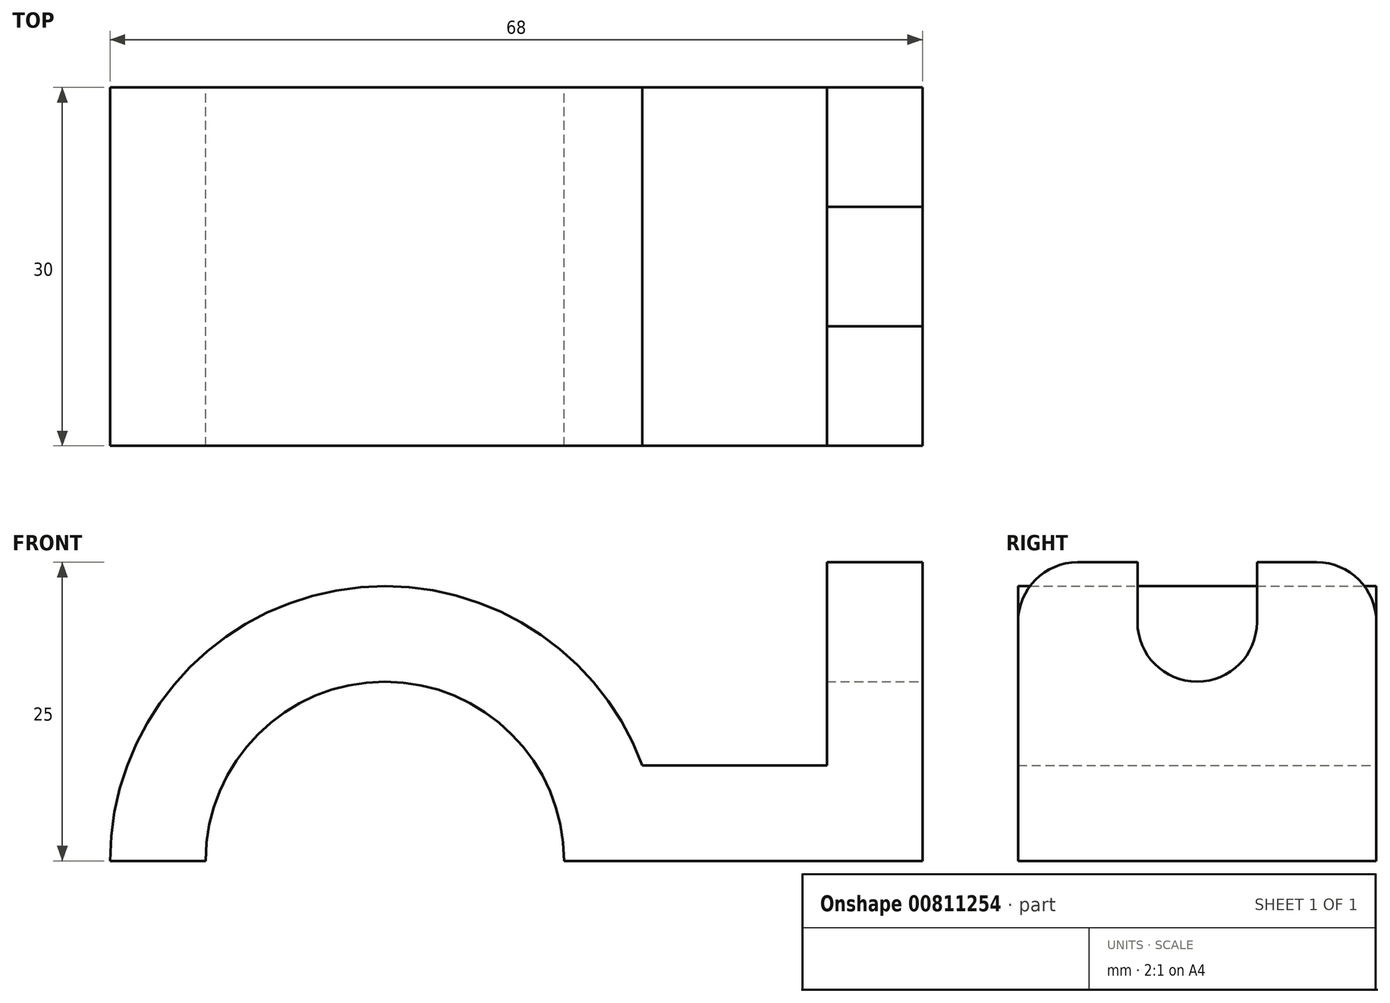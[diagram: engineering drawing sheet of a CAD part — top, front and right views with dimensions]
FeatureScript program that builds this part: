
annotation { "Feature Type Name" : "Feature", "Feature Type Description" : "" }
export const myFeature = defineFeature(function(context is Context, id is Id, definition is map)
    precondition{}
    {
        {
            var Q0;
            Q0=qCreatedBy(makeId("Front.planeOp"),FACE);
            var sketch = newSketch(context, id + "F0", { "sketchPlane" : qUnion([Q0])});
            skArc(sketch, "E0", {"start": v(15, 0) * mm, "mid": v(0, 15) * mm, "end": v(-15, 0) * mm});
            skArc(sketch, "E1", {"start": v(21.56, 8) * mm, "mid": v(-4.06, 22.64) * mm, "end": v(-23, 0) * mm});
            skLineSegment(sketch, "E2", {"start": v(-23, 0) * mm, "end": v(-15, 0) * mm});
            skLineSegment(sketch, "E3", {"start": v(45, 0) * mm, "end": v(45, 25) * mm});
            skLineSegment(sketch, "E4", {"start": v(45, 25) * mm, "end": v(37, 25) * mm});
            skLineSegment(sketch, "E5", {"start": v(37, 25) * mm, "end": v(37, 8) * mm});
            skLineSegment(sketch, "E6.trimOffspring", {"start": v(21.56, 8) * mm, "end": v(37, 8) * mm});
            skLineSegment(sketch, "E7.trimOffspring", {"start": v(15, 0) * mm, "end": v(45, 0) * mm});
            skSolve(sketch);
        }
        {
            var Q0;
            Q0 = qSketchRegion(id + "F0", true);
            extrude(context, id + "F1", {"entities" : qUnion([Q0]), "depth" : 30 * mm, "offsetDistance" : 25 * mm});
        }
        {
            var Q0;
            Q0=makeQuery(id+"F1.opExtrude","SWEPT_FACE",FACE,{"disambiguationData":[OSD([sQuery(id+"F0.wireOp",EDGE,"E3")])]});
            var sketch = newSketch(context, id + "F2", { "sketchPlane" : qUnion([Q0])});
            skLineSegment(sketch, "E8", {"start": v(-15, 0) * mm, "end": v(-15, 7.84) * mm, "construction": true});
            skLineSegment(sketch, "E9.bottom", {"start": v(-20, 25) * mm, "end": v(-10, 25) * mm});
            skLineSegment(sketch, "E9.top", {"start": v(-20, 15) * mm, "end": v(-10, 15) * mm});
            skLineSegment(sketch, "E9.left", {"start": v(-20, 25) * mm, "end": v(-20, 15) * mm});
            skLineSegment(sketch, "E9.right", {"start": v(-10, 25) * mm, "end": v(-10, 15) * mm});
            skSolve(sketch);
        }
        {
            var Q0;
            Q0 = qSketchRegion(id + "F2", true);
            var Q1;
            Q1=makeQuery(id+"F1.opExtrude","SWEPT_FACE",FACE,{"disambiguationData":[OSD([sQuery(id+"F0.wireOp",EDGE,"E5")])]});
            extrude(context, id + "F3", {"entities" : qUnion([Q0]), "operationType" : NewBodyOperationType.REMOVE, "endBound" : BoundingType.UP_TO_SURFACE, "oppositeDirection" : true, "depth" : 25 * mm, "endBoundEntityFace" : qUnion([Q1]), "offsetDistance" : 25 * mm});
        }
        {
            var Q0;
            Q0=makeQuery(id+"F1.opExtrude","CAP_EDGE",EDGE,{"disambiguationData":[OSD([sQuery(id+"F0.wireOp",EDGE,"E4")])],"isStart":false});
            var Q1;
            Q1=makeQuery(id+"F1.opExtrude","CAP_EDGE",EDGE,{"disambiguationData":[OSD([sQuery(id+"F0.wireOp",EDGE,"E4")])],"isStart":true});
            var Q2;
            Q2=makeQuery(id+"F3.boolean.opBoolean","COPY",EDGE,{"derivedFrom":makeQuery(id+"F3.opExtrude","SWEPT_EDGE",EDGE,{"disambiguationData":[OSD([sQuery(id+"F2.wireOp",EDGE,"E9.top"),sQuery(id+"F2.wireOp",EDGE,"E9.right")])]})});
            var Q3;
            Q3=makeQuery(id+"F3.boolean.opBoolean","COPY",EDGE,{"derivedFrom":makeQuery(id+"F3.opExtrude","SWEPT_EDGE",EDGE,{"disambiguationData":[OSD([sQuery(id+"F2.wireOp",EDGE,"E9.top"),sQuery(id+"F2.wireOp",EDGE,"E9.left")])]})});
            fillet(context, id + "F4", {"entities" : qUnion([Q0, Q1, Q2, Q3]), "radius" : 5 * mm, "tangentPropagation" : true, "allowEdgeOverflow" : false});
        }
    });
